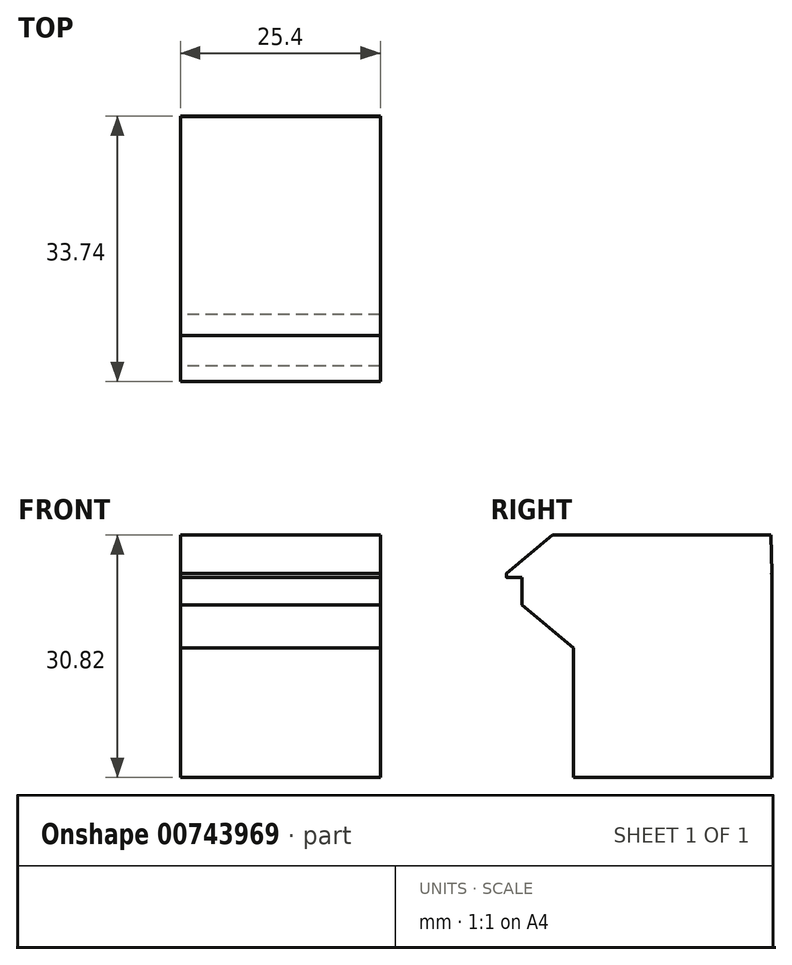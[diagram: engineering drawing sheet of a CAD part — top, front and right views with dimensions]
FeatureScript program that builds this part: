
annotation { "Feature Type Name" : "Feature", "Feature Type Description" : "" }
export const myFeature = defineFeature(function(context is Context, id is Id, definition is map)
    precondition{}
    {
        {
            var Q0;
            Q0=qCreatedBy(makeId("Right.planeOp"),FACE);
            var sketch = newSketch(context, id + "F0", { "sketchPlane" : qUnion([Q0])});
            skPoint(sketch, "E0.middle", {"position": v(0, 0) * mm});
            skLineSegment(sketch, "E1", {"start": v(-14.6, 8.92) * mm, "end": v(-14.6, 5.49) * mm});
            skLineSegment(sketch, "E2", {"start": v(-14.6, 5.49) * mm, "end": v(-14.6, 8.92) * mm});
            skLineSegment(sketch, "E3", {"start": v(-14.6, 5.49) * mm, "end": v(-8.05, 0) * mm});
            skLineSegment(sketch, "E4", {"start": v(-8.05, 0) * mm, "end": v(-8.05, -16.48) * mm});
            skLineSegment(sketch, "E5", {"start": v(-8.05, -16.48) * mm, "end": v(17.16, -16.48) * mm});
            skLineSegment(sketch, "E6", {"start": v(17.16, -16.48) * mm, "end": v(17.16, 8.92) * mm});
            skLineSegment(sketch, "E7", {"start": v(17.16, 9.02) * mm, "end": v(17.16, 9.34) * mm});
            skLineSegment(sketch, "E8", {"start": v(-16.58, 9.02) * mm, "end": v(-16.58, 9.34) * mm});
            skLineSegment(sketch, "E9", {"start": v(-16.49, 9.43) * mm, "end": v(17.06, 9.43) * mm});
            skPoint(sketch, "E10.visualSharp", {"position": v(-16.58, 9.43) * mm});
            skArc(sketch, "E10.filletArc", {"start": v(-16.49, 9.43) * mm, "mid": v(-16.56, 9.4) * mm, "end": v(-16.58, 9.34) * mm});
            skPoint(sketch, "E11.visualSharp", {"position": v(17.16, 9.43) * mm});
            skArc(sketch, "E11.filletArc", {"start": v(17.16, 9.34) * mm, "mid": v(17.13, 9.4) * mm, "end": v(17.06, 9.43) * mm});
            skPoint(sketch, "E12.visualSharp", {"position": v(17.16, 8.92) * mm});
            skArc(sketch, "E12.filletArc", {"start": v(17.06, 8.92) * mm, "mid": v(17.13, 8.95) * mm, "end": v(17.16, 9.02) * mm});
            skPoint(sketch, "E13.visualSharp", {"position": v(-16.58, 8.92) * mm});
            skArc(sketch, "E13.filletArc", {"start": v(-16.58, 9.02) * mm, "mid": v(-16.56, 8.95) * mm, "end": v(-16.49, 8.92) * mm});
            skLineSegment(sketch, "E14", {"start": v(-16.58, 8.92) * mm, "end": v(17.16, 8.92) * mm});
            skLineSegment(sketch, "E15", {"start": v(17.16, 9.43) * mm, "end": v(17.06, 14.34) * mm});
            skLineSegment(sketch, "E16", {"start": v(17.06, 14.34) * mm, "end": v(-10.74, 14.34) * mm});
            skLineSegment(sketch, "E17", {"start": v(-10.74, 14.34) * mm, "end": v(-16.58, 9.43) * mm});
            skLineSegment(sketch, "E18", {"start": v(-16.49, 9.43) * mm, "end": v(-16.58, 9.43) * mm});
            skLineSegment(sketch, "E19", {"start": v(17.16, 9.43) * mm, "end": v(-16.58, 9.43) * mm});
            skSolve(sketch);
        }
        {
            var Q0;
            Q0=makeQuery(id+"F0.imprint","IMPRINT",FACE,{"disambiguationData":[TD([[makeQuery(id+"F0.imprint","IMPRINT",EDGE,{"derivedFrom":sQuery(id+"F0.wireOp",EDGE,"E9")}),1.0]])]});
            extrude(context, id + "F1", {"entities" : qUnion([Q0]), "depth" : 25.4 * mm, "offsetDistance" : 25.4 * mm});
        }
        {
            var Q0;
            Q0=makeQuery(id+"F0.imprint","IMPRINT",FACE,{"disambiguationData":[TD([[makeQuery(id+"F0.imprint","IMPRINT",EDGE,{"derivedFrom":sQuery(id+"F0.wireOp",EDGE,"E7")}),1.0]])]});
            extrude(context, id + "F2", {"entities" : qUnion([Q0]), "operationType" : NewBodyOperationType.ADD, "depth" : 25.4 * mm, "offsetDistance" : 25.4 * mm});
        }
        {
            var Q0;
            {var subQ3=sQuery(id+"F0.wireOp",EDGE,"E1");Q0=makeQuery(id+"F0.imprint","IMPRINT",FACE,{"disambiguationData":[TD([[makeQuery(id+"F0.imprint","IMPRINT",EDGE,{"derivedFrom":subQ3}),1.0]])]});}
            extrude(context, id + "F3", {"entities" : qUnion([Q0]), "operationType" : NewBodyOperationType.ADD, "depth" : 25.4 * mm, "offsetDistance" : 25.4 * mm});
        }
    });
